# Revit family: Sink-Undermount-Acorn-SUADA-2116-45,55_Series
name_source: partatom
category: Plumbing Fixtures
units: mm (PartAtom-declared; Revit-internal decimal feet)

## family parameters
Cut with Voids When Loaded = No
Host = Face
OmniClass Number = 23.45.05.14.14
OmniClass Title = Sinks/Lavatories
Part Type = Normal
Room Calculation Point = No
Round Connector Dimension = Use Diameter
Shared = Yes

## types (2) — shared parameters
ADA Compliant = Yes
Assembly Code = D2010440
Bowl Length = 15 3/4"
Bowl Width = 21"
CW Connection = No
CWFU = 3
Compliance Certifications = ASME A112.19.3/CSA B45.4, IAPMO® Certified
Default Elevation = 34"
Description = Stainless Steel Undermount Sink
Drain Opening Size = 3 1/2"
Finish = Stainless Steel-Acorn-Satin
HW Connection = No
HWFU = 3
Installation Type = Wall Mounted
Length = 18 1/4"
Manufacturer = Acorn
Material = Stainless Steel-Acorn-Satin
URL = https://www.acorneng.com
Vent Connection = No
WFU = 4
Waste Connection = No
Width = 23 1/2"
cUPC Compliant = Yes

## per-type parameters (varying)
| type | Height |
| SUADA-2116-55 | 5 1/2" |
| SUADA-2116-45 | 4 1/2" |

note: column(s) folded — value = type name in every type: Model

## geometry (parser evidence)
native form markers: Sweep x3
no freeform markers — native parametric forms only
